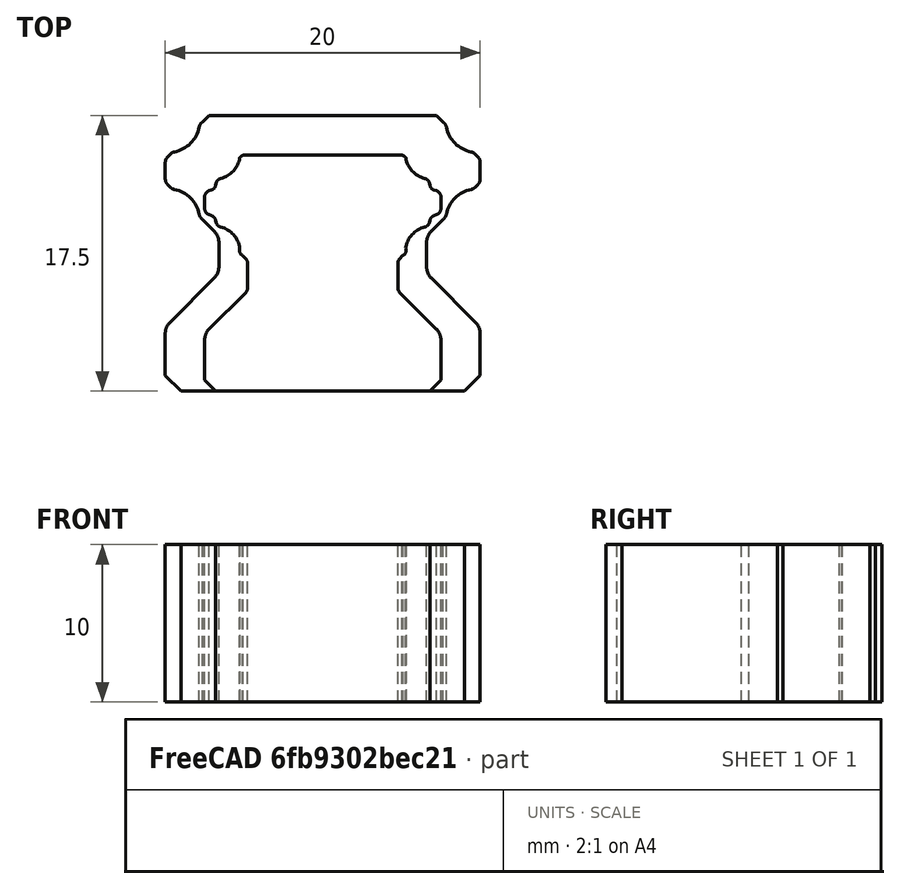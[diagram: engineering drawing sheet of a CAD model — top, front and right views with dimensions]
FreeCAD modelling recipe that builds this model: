
FCSTD DOCUMENT  (FreeCAD 0.20R30923 (Git))
Label: HGxx_temp
License: All rights reserved
LicenseURL: http://en.wikipedia.org/wiki/All_rights_reserved
objects: Sketcher::SketchObject×3, PartDesign::Body×3, App::FeaturePython×2, Part::FeaturePython×2, PartDesign::Pad×2, App::Link×1, Spreadsheet::Sheet×1
note: 13 computed .brp shape members not serialized (recipe doc carries the construction recipe); baked Part::Feature solids carry a one-line shape summary decoded from their .brp

FEATURE [Sketcher::SketchObject] Sketch  label="HGR25R"
  FullyConstrained = false
  TreeRank = 161
  sketch-geometry (46):
    g0: LineSegment StartX=11.2096 StartY=6.56184 StartZ=0 EndX=8.20598 EndY=9.58663 EndZ=0
    g1: LineSegment StartX=-9.97922 StartY=0 StartZ=0 EndX=-11.5 EndY=1.52786 EndZ=0
    g2: LineSegment StartX=-8.20846 StartY=13.8135 StartZ=0 EndX=-8.93873 EndY=14.5438 EndZ=0
    g3: LineSegment StartX=2.10672 StartY=0 StartZ=0 EndX=1.58064 EndY=0.526074 EndZ=0
    g4: LineSegment StartX=-11.2036 StartY=16.7216 StartZ=0 EndX=-11.3536 EndY=16.8716 EndZ=0
    g5: LineSegment StartX=11.3536 StartY=18.9781 StartZ=0 EndX=11.1895 EndY=19.1421 EndZ=0
    g6: LineSegment StartX=9.04575 StartY=21.2544 StartZ=0 EndX=8.30011 EndY=22 EndZ=0
    g7: LineSegment StartX=-9.97922 StartY=0 StartZ=0 EndX=-2.10672 EndY=0 EndZ=0
    g8: LineSegment StartX=2.10672 StartY=0 StartZ=0 EndX=9.97922 EndY=0 EndZ=0
    g9: LineSegment StartX=-1.58064 StartY=0.526074 StartZ=0 EndX=1.58064 EndY=0.526074 EndZ=0
    g10: LineSegment StartX=-8.30011 StartY=22 StartZ=0 EndX=8.30011 EndY=22 EndZ=0
    g11: LineSegment StartX=-2.10672 StartY=0 StartZ=0 EndX=-1.58064 EndY=0.526074 EndZ=0
    g12: LineSegment StartX=11.2036 StartY=16.7216 StartZ=0 EndX=11.3536 EndY=16.8716 EndZ=0
    g13: LineSegment StartX=-11.3536 StartY=18.9781 StartZ=0 EndX=-11.1895 EndY=19.1421 EndZ=0
    g14: LineSegment StartX=-9.04575 StartY=21.2544 StartZ=0 EndX=-8.30011 EndY=22 EndZ=0
    g15: LineSegment StartX=8.20846 StartY=13.8135 StartZ=0 EndX=8.93873 EndY=14.5438 EndZ=0
    g16: LineSegment StartX=9.97922 StartY=0 StartZ=0 EndX=11.5 EndY=1.52786 EndZ=0
    g17: LineSegment StartX=-11.2096 StartY=6.56184 StartZ=0 EndX=-8.20598 EndY=9.58663 EndZ=0
    g18: LineSegment StartX=-11.5 StartY=17.2251 StartZ=0 EndX=-11.5 EndY=18.6245 EndZ=0
    g19: LineSegment StartX=-11.5 StartY=1.52786 StartZ=0 EndX=-11.5 EndY=5.85723 EndZ=0
    g20: LineSegment StartX=-7.91557 StartY=10.2912 StartZ=0 EndX=-7.91557 EndY=13.1064 EndZ=0
    g21: LineSegment StartX=7.91557 StartY=10.2912 StartZ=0 EndX=7.91557 EndY=13.1064 EndZ=0
    g22: LineSegment StartX=11.5 StartY=1.52786 StartZ=0 EndX=11.5 EndY=5.85723 EndZ=0
    g23: LineSegment StartX=11.5 StartY=17.2251 StartZ=0 EndX=11.5 EndY=18.6245 EndZ=0
    g24: ArcOfCircle CenterX=-11.4771 CenterY=14.2438 CenterZ=0 NormalX=0 NormalY=0 NormalZ=1 AngleXU=0 Radius=2.4 StartAngle=0.218097 EndAngle=1.35284
    g25: ArcOfCircle CenterX=-11.4693 CenterY=21.6085 CenterZ=0 NormalX=0 NormalY=0 NormalZ=1 AngleXU=0 Radius=2.4 StartAngle=4.93215 EndAngle=6.08802
    g26: ArcOfCircle CenterX=-11 CenterY=17.2251 CenterZ=0 NormalX=0 NormalY=0 NormalZ=1 AngleXU=0 Radius=0.5 StartAngle=3.14159 EndAngle=3.92699
    g27: ArcOfCircle CenterX=-11 CenterY=18.6245 CenterZ=0 NormalX=0 NormalY=0 NormalZ=1 AngleXU=0 Radius=0.499999 StartAngle=2.3562 EndAngle=3.14159
    g28: ArcOfCircle CenterX=-10.85 CenterY=17.0752 CenterZ=0 NormalX=0 NormalY=0 NormalZ=1 AngleXU=0 Radius=0.5 StartAngle=3.92699 EndAngle=4.49444
    g29: ArcOfCircle CenterX=-10.8494 CenterY=18.7757 CenterZ=0 NormalX=0 NormalY=0 NormalZ=1 AngleXU=0 Radius=0.5 StartAngle=1.76548 EndAngle=2.31906
    g30: ArcOfCircle CenterX=-10.5 CenterY=5.85723 CenterZ=0 NormalX=0 NormalY=0 NormalZ=1 AngleXU=0 Radius=0.999997 StartAngle=2.35971 EndAngle=3.14159
    g31: ArcOfCircle CenterX=-8.91557 CenterY=13.1064 CenterZ=0 NormalX=0 NormalY=0 NormalZ=1 AngleXU=0 Radius=1 StartAngle=0 EndAngle=0.785398
    g32: ArcOfCircle CenterX=-8.91557 CenterY=10.2912 CenterZ=0 NormalX=0 NormalY=0 NormalZ=1 AngleXU=0 Radius=0.999997 StartAngle=5.5013 EndAngle=6.28319
    g33: ArcOfCircle CenterX=-8.67937 CenterY=14.9712 CenterZ=0 NormalX=0 NormalY=0 NormalZ=1 AngleXU=0 Radius=0.5 StartAngle=3.57106 EndAngle=4.16705
    g34: ArcOfCircle CenterX=-8.6749 CenterY=20.9471 CenterZ=0 NormalX=0 NormalY=0 NormalZ=1 AngleXU=0 Radius=0.48161 StartAngle=2.44968 EndAngle=2.72251
    g35: ArcOfCircle CenterX=8.6749 CenterY=20.9471 CenterZ=0 NormalX=0 NormalY=0 NormalZ=1 AngleXU=0 Radius=0.481608 StartAngle=0.419083 EndAngle=0.691918
    g36: ArcOfCircle CenterX=8.67937 CenterY=14.9712 CenterZ=0 NormalX=0 NormalY=0 NormalZ=1 AngleXU=0 Radius=0.5 StartAngle=5.25773 EndAngle=5.85371
    g37: ArcOfCircle CenterX=8.91557 CenterY=10.2912 CenterZ=0 NormalX=0 NormalY=0 NormalZ=1 AngleXU=0 Radius=0.999997 StartAngle=3.14159 EndAngle=3.92348
    g38: ArcOfCircle CenterX=8.91557 CenterY=13.1064 CenterZ=0 NormalX=0 NormalY=0 NormalZ=1 AngleXU=0 Radius=1 StartAngle=2.35619 EndAngle=3.14159
    g39: ArcOfCircle CenterX=10.5 CenterY=5.85723 CenterZ=0 NormalX=0 NormalY=0 NormalZ=1 AngleXU=0 Radius=0.999997 StartAngle=0 EndAngle=0.781885
    g40: ArcOfCircle CenterX=10.8494 CenterY=18.7757 CenterZ=0 NormalX=0 NormalY=0 NormalZ=1 AngleXU=0 Radius=0.5 StartAngle=0.82253 EndAngle=1.37611
    g41: ArcOfCircle CenterX=10.85 CenterY=17.0752 CenterZ=0 NormalX=0 NormalY=0 NormalZ=1 AngleXU=0 Radius=0.5 StartAngle=4.93034 EndAngle=5.49779
    g42: ArcOfCircle CenterX=11 CenterY=17.2251 CenterZ=0 NormalX=0 NormalY=0 NormalZ=1 AngleXU=0 Radius=0.499999 StartAngle=5.49779 EndAngle=6.28319
    g43: ArcOfCircle CenterX=11 CenterY=18.6245 CenterZ=0 NormalX=0 NormalY=0 NormalZ=1 AngleXU=0 Radius=0.5 StartAngle=6.28318 EndAngle=7.06858
    g44: ArcOfCircle CenterX=11.4693 CenterY=21.6085 CenterZ=0 NormalX=0 NormalY=0 NormalZ=1 AngleXU=0 Radius=2.4 StartAngle=3.33676 EndAngle=4.49263
    g45: ArcOfCircle CenterX=11.4771 CenterY=14.2438 CenterZ=0 NormalX=0 NormalY=0 NormalZ=1 AngleXU=0 Radius=2.4 StartAngle=1.78875 EndAngle=2.9235
FEATURE [Sketcher::SketchObject] Sketch001  label="HGR20R"
  FullyConstrained = false
  TreeRank = 159
  sketch-geometry (42):
    g0: LineSegment StartX=-9 StartY=0 StartZ=0 EndX=-10 EndY=1 EndZ=0
    g1: LineSegment StartX=9.70711 StartY=4.36361 StartZ=0 EndX=6.89289 EndY=7.17783 EndZ=0
    g2: LineSegment StartX=-9.69063 StartY=12.9499 StartZ=0 EndX=-9.85355 EndY=13.1128 EndZ=0
    g3: LineSegment StartX=7.63253 StartY=17.0982 StartZ=0 EndX=7.23072 EndY=17.5 EndZ=0
    g4: LineSegment StartX=-6.89289 StartY=10.1522 StartZ=0 EndX=-7.63016 EndY=10.8894 EndZ=0
    g5: LineSegment StartX=9.85355 StartY=14.8772 StartZ=0 EndX=9.6785 EndY=15.0522 EndZ=0
    g6: LineSegment StartX=-9 StartY=0 StartZ=0 EndX=9 EndY=0 EndZ=0
    g7: LineSegment StartX=-7.23072 StartY=17.5 StartZ=0 EndX=7.23072 EndY=17.5 EndZ=0
    g8: LineSegment StartX=-9.85355 StartY=14.8772 StartZ=0 EndX=-9.6785 EndY=15.0522 EndZ=0
    g9: LineSegment StartX=6.89289 StartY=10.1522 StartZ=0 EndX=7.63016 EndY=10.8894 EndZ=0
    g10: LineSegment StartX=9 StartY=0 StartZ=0 EndX=10 EndY=1 EndZ=0
    g11: LineSegment StartX=-9.70711 StartY=4.36361 StartZ=0 EndX=-6.89289 EndY=7.17783 EndZ=0
    g12: LineSegment StartX=9.69063 StartY=12.9499 StartZ=0 EndX=9.85355 EndY=13.1128 EndZ=0
    g13: LineSegment StartX=-7.63253 StartY=17.0982 StartZ=0 EndX=-7.23072 EndY=17.5 EndZ=0
    g14: LineSegment StartX=-10 StartY=1 StartZ=0 EndX=-10 EndY=3.65651 EndZ=0
    g15: LineSegment StartX=-10 StartY=13.4664 StartZ=0 EndX=-10 EndY=14.5236 EndZ=0
    g16: LineSegment StartX=-6.6 StartY=7.88493 StartZ=0 EndX=-6.6 EndY=9.44506 EndZ=0
    g17: LineSegment StartX=6.6 StartY=7.88493 StartZ=0 EndX=6.6 EndY=9.44507 EndZ=0
    g18: LineSegment StartX=10 StartY=1 StartZ=0 EndX=10 EndY=3.65651 EndZ=0
    g19: LineSegment StartX=10 StartY=13.4664 StartZ=0 EndX=10 EndY=14.5236 EndZ=0
    g20: ArcOfCircle CenterX=-9.8106 CenterY=10.8487 CenterZ=0 NormalX=0 NormalY=0 NormalZ=1 AngleXU=0 Radius=2 StartAngle=0.190564 EndAngle=1.38023
    g21: ArcOfCircle CenterX=-9.81014 CenterY=17.1511 CenterZ=0 NormalX=0 NormalY=0 NormalZ=1 AngleXU=0 Radius=2 StartAngle=4.9077 EndAngle=6.08787
    g22: ArcOfCircle CenterX=-9.5 CenterY=13.4664 CenterZ=0 NormalX=0 NormalY=0 NormalZ=1 AngleXU=0 Radius=0.499999 StartAngle=3.14159 EndAngle=3.92699
    g23: ArcOfCircle CenterX=-9.5 CenterY=14.5236 CenterZ=0 NormalX=0 NormalY=0 NormalZ=1 AngleXU=0 Radius=0.499999 StartAngle=2.3562 EndAngle=3.14159
    g24: ArcOfCircle CenterX=-9.33707 CenterY=13.3035 CenterZ=0 NormalX=0 NormalY=0 NormalZ=1 AngleXU=0 Radius=0.499999 StartAngle=3.92699 EndAngle=4.52183
    g25: ArcOfCircle CenterX=-9.32495 CenterY=14.6987 CenterZ=0 NormalX=0 NormalY=0 NormalZ=1 AngleXU=0 Radius=0.500001 StartAngle=1.76611 EndAngle=2.3562
    g26: ArcOfCircle CenterX=-9 CenterY=3.65651 CenterZ=0 NormalX=0 NormalY=0 NormalZ=1 AngleXU=0 Radius=1 StartAngle=2.35619 EndAngle=3.14159
    g27: ArcOfCircle CenterX=-7.6 CenterY=7.88493 CenterZ=0 NormalX=0 NormalY=0 NormalZ=1 AngleXU=0 Radius=1 StartAngle=5.49779 EndAngle=6.28319
    g28: ArcOfCircle CenterX=-7.6 CenterY=9.44506 CenterZ=0 NormalX=0 NormalY=0 NormalZ=1 AngleXU=0 Radius=1 StartAngle=0 EndAngle=0.785399
    g29: ArcOfCircle CenterX=-7.35468 CenterY=16.6825 CenterZ=0 NormalX=0 NormalY=0 NormalZ=1 AngleXU=0 Radius=0.5 StartAngle=2.16 EndAngle=2.97992
    g30: ArcOfCircle CenterX=-7.35293 CenterY=11.3055 CenterZ=0 NormalX=0 NormalY=0 NormalZ=1 AngleXU=0 Radius=0.5 StartAngle=3.29825 EndAngle=4.12467
    g31: ArcOfCircle CenterX=7.35293 CenterY=11.3055 CenterZ=0 NormalX=0 NormalY=0 NormalZ=1 AngleXU=0 Radius=0.5 StartAngle=5.30011 EndAngle=6.12653
    g32: ArcOfCircle CenterX=7.35468 CenterY=16.6825 CenterZ=0 NormalX=0 NormalY=0 NormalZ=1 AngleXU=0 Radius=0.500001 StartAngle=0.161676 EndAngle=0.981596
    g33: ArcOfCircle CenterX=7.6 CenterY=7.88493 CenterZ=0 NormalX=0 NormalY=0 NormalZ=1 AngleXU=0 Radius=1 StartAngle=3.14159 EndAngle=3.92699
    g34: ArcOfCircle CenterX=7.6 CenterY=9.44507 CenterZ=0 NormalX=0 NormalY=0 NormalZ=1 AngleXU=0 Radius=1 StartAngle=2.35619 EndAngle=3.14159
    g35: ArcOfCircle CenterX=9 CenterY=3.65651 CenterZ=0 NormalX=0 NormalY=0 NormalZ=1 AngleXU=0 Radius=1 StartAngle=0 EndAngle=0.785398
    g36: ArcOfCircle CenterX=9.32495 CenterY=14.6987 CenterZ=0 NormalX=0 NormalY=0 NormalZ=1 AngleXU=0 Radius=0.499999 StartAngle=0.785397 EndAngle=1.37548
    g37: ArcOfCircle CenterX=9.33707 CenterY=13.3035 CenterZ=0 NormalX=0 NormalY=0 NormalZ=1 AngleXU=0 Radius=0.5 StartAngle=4.90295 EndAngle=5.49779
    g38: ArcOfCircle CenterX=9.5 CenterY=13.4664 CenterZ=0 NormalX=0 NormalY=0 NormalZ=1 AngleXU=0 Radius=0.499999 StartAngle=5.49779 EndAngle=6.28319
    g39: ArcOfCircle CenterX=9.5 CenterY=14.5236 CenterZ=0 NormalX=0 NormalY=0 NormalZ=1 AngleXU=0 Radius=0.499999 StartAngle=0 EndAngle=0.785397
    g40: ArcOfCircle CenterX=9.81014 CenterY=17.1511 CenterZ=0 NormalX=0 NormalY=0 NormalZ=1 AngleXU=0 Radius=2 StartAngle=3.33691 EndAngle=4.51707
    g41: ArcOfCircle CenterX=9.8106 CenterY=10.8487 CenterZ=0 NormalX=0 NormalY=0 NormalZ=1 AngleXU=0 Radius=2 StartAngle=1.76136 EndAngle=2.95103
  constraints (50):
    c: Coincident(g7,g13)
    c: Coincident(g13,g29)
    c: Coincident(g21,g29)
    c: Coincident(g21,g25)
    c: Coincident(g8,g25)
    c: Coincident(g8,g23)
    c: Coincident(g15,g23)
    c: Coincident(g15,g22)
    c: Coincident(g2,g22)
    c: Coincident(g2,g24)
    c: Coincident(g20,g24)
    c: Coincident(g20,g30)
    c: Coincident(g4,g30)
    c: Coincident(g4,g28)
    c: Coincident(g16,g28)
    c: Coincident(g16,g27)
    c: Coincident(g11,g27)
    c: Coincident(g11,g26)
    c: Coincident(g14,g26)
    c: Coincident(g0,g14)
    c: Coincident(g0,g6)
    c: Coincident(g6,g10)
    c: Coincident(g10,g18)
    c: Coincident(g18,g35)
    c: Coincident(g1,g35)
    c: Coincident(g1,g33)
    c: Coincident(g17,g33)
    c: Coincident(g17,g34)
    c: Coincident(g9,g34)
    c: Coincident(g9,g31)
    c: Coincident(g31,g41)
    c: Coincident(g37,g41)
    c: Coincident(g12,g37)
    c: Coincident(g12,g38)
    c: Coincident(g19,g38)
    c: Coincident(g19,g39)
    c: Coincident(g5,g39)
    c: Coincident(g5,g36)
    c: Coincident(g36,g40)
    c: Coincident(g32,g40)
    c: Coincident(g3,g32)
    c: Coincident(g3,g7)
    c: Horizontal(g7)
    c: Vertical(g19)
    c: Vertical(g18)
    c: Horizontal(g6)
    c: Vertical(g16)
    c: Vertical(g17)
    c: Vertical(g14)
    c: Vertical(g15)
FEATURE [Sketcher::SketchObject] Sketch002  label="HGR15R"
  FullyConstrained = false
  TreeRank = 158
  sketch-geometry (50):
    g0: LineSegment StartX=6.80531 StartY=13.0612 StartZ=0 EndX=6.77501 EndY=13.2021 EndZ=0
    g1: LineSegment StartX=-6.77426 StartY=10.7128 StartZ=0 EndX=-6.80624 EndY=10.8541 EndZ=0
    g2: LineSegment StartX=-6.8 StartY=0 StartZ=0 EndX=-7.5 EndY=0.7 EndZ=0
    g3: LineSegment StartX=7.20711 StartY=3.95047 StartZ=0 EndX=4.88716 EndY=6.27042 EndZ=0
    g4: LineSegment StartX=-4.88716 StartY=8.39816 StartZ=0 EndX=-5.08159 EndY=8.59259 EndZ=0
    g5: LineSegment StartX=5.08606 StartY=14.9629 StartZ=0 EndX=5.04899 EndY=15 EndZ=0
    g6: LineSegment StartX=-7.06065 StartY=11.1421 StartZ=0 EndX=-7.23572 EndY=11.2052 EndZ=0
    g7: LineSegment StartX=7.21871 StartY=12.7195 StartZ=0 EndX=7.07767 EndY=12.7633 EndZ=0
    g8: LineSegment StartX=-6.8 StartY=0 StartZ=0 EndX=6.8 EndY=0 EndZ=0
    g9: LineSegment StartX=-5.04899 StartY=15 StartZ=0 EndX=5.04899 EndY=15 EndZ=0
    g10: LineSegment StartX=-7.21871 StartY=12.7195 StartZ=0 EndX=-7.07767 EndY=12.7633 EndZ=0
    g11: LineSegment StartX=7.06065 StartY=11.1421 StartZ=0 EndX=7.23572 EndY=11.2052 EndZ=0
    g12: LineSegment StartX=6.8 StartY=0 StartZ=0 EndX=7.5 EndY=0.7 EndZ=0
    g13: LineSegment StartX=-7.20711 StartY=3.95047 StartZ=0 EndX=-4.88716 EndY=6.27042 EndZ=0
    g14: LineSegment StartX=4.88716 StartY=8.39816 StartZ=0 EndX=5.08159 EndY=8.59259 EndZ=0
    g15: LineSegment StartX=-5.08606 StartY=14.9629 StartZ=0 EndX=-5.04899 EndY=15 EndZ=0
    g16: LineSegment StartX=6.77426 StartY=10.7128 StartZ=0 EndX=6.80623 EndY=10.8541 EndZ=0
    g17: LineSegment StartX=-6.80531 StartY=13.0612 StartZ=0 EndX=-6.77501 EndY=13.2021 EndZ=0
    g18: LineSegment StartX=-7.5 StartY=0.7 StartZ=0 EndX=-7.5 EndY=3.24336 EndZ=0
    g19: LineSegment StartX=-7.5 StartY=11.5815 StartZ=0 EndX=-7.5 EndY=12.3375 EndZ=0
    g20: LineSegment StartX=-4.77 StartY=6.55326 StartZ=0 EndX=-4.77 EndY=8.11532 EndZ=0
    g21: LineSegment StartX=4.77 StartY=6.55326 StartZ=0 EndX=4.77 EndY=8.11532 EndZ=0
    g22: LineSegment StartX=7.5 StartY=0.7 StartZ=0 EndX=7.5 EndY=3.24336 EndZ=0
    g23: LineSegment StartX=7.5 StartY=11.5815 StartZ=0 EndX=7.5 EndY=12.3375 EndZ=0
    g24: ArcOfCircle CenterX=-7.19637 CenterY=10.7658 CenterZ=0 NormalX=0 NormalY=0 NormalZ=1 AngleXU=0 Radius=0.4 StartAngle=0.222511 EndAngle=1.22461
    g25: ArcOfCircle CenterX=-7.19637 CenterY=13.1453 CenterZ=0 NormalX=0 NormalY=0 NormalZ=1 AngleXU=0 Radius=0.399999 StartAngle=5.01369 EndAngle=6.07137
    g26: ArcOfCircle CenterX=-7.1 CenterY=11.5815 CenterZ=0 NormalX=0 NormalY=0 NormalZ=1 AngleXU=0 Radius=0.4 StartAngle=3.14159 EndAngle=4.3662
    g27: ArcOfCircle CenterX=-7.1 CenterY=12.3375 CenterZ=0 NormalX=0 NormalY=0 NormalZ=1 AngleXU=0 Radius=0.399999 StartAngle=1.8721 EndAngle=3.14159
    g28: ArcOfCircle CenterX=-6.85624 CenterY=8.85756 CenterZ=0 NormalX=0 NormalY=0 NormalZ=1 AngleXU=0 Radius=1.6 StartAngle=0.134276 EndAngle=1.33249
    g29: ArcOfCircle CenterX=-6.85623 CenterY=15.0614 CenterZ=0 NormalX=0 NormalY=0 NormalZ=1 AngleXU=0 Radius=1.6 StartAngle=4.95078 EndAngle=6.13385
    g30: ArcOfCircle CenterX=-6.5 CenterY=3.24336 CenterZ=0 NormalX=0 NormalY=0 NormalZ=1 AngleXU=0 Radius=1 StartAngle=2.35619 EndAngle=3.14159
    g31: ArcOfCircle CenterX=-6.38412 CenterY=10.801 CenterZ=0 NormalX=0 NormalY=0 NormalZ=1 AngleXU=0 Radius=0.4 StartAngle=3.3641 EndAngle=4.47408
    g32: ArcOfCircle CenterX=-6.38395 CenterY=13.118 CenterZ=0 NormalX=0 NormalY=0 NormalZ=1 AngleXU=0 Radius=0.4 StartAngle=1.80919 EndAngle=2.92978
    g33: ArcOfCircle CenterX=-5.17 CenterY=6.55326 CenterZ=0 NormalX=0 NormalY=0 NormalZ=1 AngleXU=0 Radius=0.4 StartAngle=5.49779 EndAngle=6.28319
    g34: ArcOfCircle CenterX=-5.17 CenterY=8.11532 CenterZ=0 NormalX=0 NormalY=0 NormalZ=1 AngleXU=0 Radius=0.4 StartAngle=0 EndAngle=0.785398
    g35: ArcOfCircle CenterX=-4.95206 CenterY=14.586 CenterZ=0 NormalX=0 NormalY=0 NormalZ=1 AngleXU=0 Radius=0.4 StartAngle=1.91239 EndAngle=2.50636
    g36: ArcOfCircle CenterX=-4.89142 CenterY=8.9445 CenterZ=0 NormalX=0 NormalY=0 NormalZ=1 AngleXU=0 Radius=0.4 StartAngle=2.81782 EndAngle=4.21695
    g37: ArcOfCircle CenterX=4.89142 CenterY=8.9445 CenterZ=0 NormalX=0 NormalY=0 NormalZ=1 AngleXU=0 Radius=0.4 StartAngle=5.20783 EndAngle=6.60695
    g38: ArcOfCircle CenterX=4.95206 CenterY=14.586 CenterZ=0 NormalX=0 NormalY=0 NormalZ=1 AngleXU=0 Radius=0.4 StartAngle=0.635234 EndAngle=1.2292
    g39: ArcOfCircle CenterX=5.17 CenterY=6.55326 CenterZ=0 NormalX=0 NormalY=0 NormalZ=1 AngleXU=0 Radius=0.4 StartAngle=3.14159 EndAngle=3.92699
    g40: ArcOfCircle CenterX=5.17 CenterY=8.11532 CenterZ=0 NormalX=0 NormalY=0 NormalZ=1 AngleXU=0 Radius=0.4 StartAngle=2.3562 EndAngle=3.14159
    g41: ArcOfCircle CenterX=6.38395 CenterY=13.118 CenterZ=0 NormalX=0 NormalY=0 NormalZ=1 AngleXU=0 Radius=0.399999 StartAngle=0.211816 EndAngle=1.33241
    g42: ArcOfCircle CenterX=6.38412 CenterY=10.801 CenterZ=0 NormalX=0 NormalY=0 NormalZ=1 AngleXU=0 Radius=0.4 StartAngle=4.9507 EndAngle=6.06068
    g43: ArcOfCircle CenterX=6.5 CenterY=3.24336 CenterZ=0 NormalX=0 NormalY=0 NormalZ=1 AngleXU=0 Radius=1 StartAngle=0 EndAngle=0.785398
    g44: ArcOfCircle CenterX=6.85623 CenterY=15.0614 CenterZ=0 NormalX=0 NormalY=0 NormalZ=1 AngleXU=0 Radius=1.6 StartAngle=3.29093 EndAngle=4.474
    g45: ArcOfCircle CenterX=6.85624 CenterY=8.85756 CenterZ=0 NormalX=0 NormalY=0 NormalZ=1 AngleXU=0 Radius=1.6 StartAngle=1.8091 EndAngle=3.00732
    g46: ArcOfCircle CenterX=7.1 CenterY=11.5815 CenterZ=0 NormalX=0 NormalY=0 NormalZ=1 AngleXU=0 Radius=0.4 StartAngle=5.05857 EndAngle=6.28319
    g47: ArcOfCircle CenterX=7.1 CenterY=12.3375 CenterZ=0 NormalX=0 NormalY=0 NormalZ=1 AngleXU=0 Radius=0.4 StartAngle=1.15308e-06 EndAngle=1.2695
    g48: ArcOfCircle CenterX=7.19637 CenterY=10.7658 CenterZ=0 NormalX=0 NormalY=0 NormalZ=1 AngleXU=0 Radius=0.4 StartAngle=1.91698 EndAngle=2.91908
    g49: ArcOfCircle CenterX=7.19637 CenterY=13.1453 CenterZ=0 NormalX=0 NormalY=0 NormalZ=1 AngleXU=0 Radius=0.4 StartAngle=3.35341 EndAngle=4.41109
  constraints (50):
    c: Coincident(g9,g15)
    c: Coincident(g15,g35)
    c: Coincident(g29,g35)
    c: Coincident(g29,g32)
    c: Coincident(g17,g32)
    c: Coincident(g17,g25)
    c: Coincident(g10,g25)
    c: Coincident(g10,g27)
    c: Coincident(g19,g27)
    c: Coincident(g19,g26)
    c: Coincident(g6,g26)
    c: Coincident(g6,g24)
    c: Coincident(g1,g24)
    c: Coincident(g1,g31)
    c: Coincident(g28,g31)
    c: Coincident(g28,g36)
    c: Coincident(g4,g36)
    c: Coincident(g4,g34)
    c: Coincident(g20,g34)
    c: Coincident(g20,g33)
    c: Coincident(g13,g33)
    c: Coincident(g13,g30)
    c: Coincident(g18,g30)
    c: Coincident(g2,g18)
    c: Coincident(g2,g8)
    c: Coincident(g8,g12)
    c: Coincident(g12,g22)
    c: Coincident(g22,g43)
    c: Coincident(g3,g43)
    c: Coincident(g3,g39)
    c: Coincident(g21,g39)
    c: Coincident(g21,g40)
    c: Coincident(g14,g40)
    c: Coincident(g14,g37)
    c: Coincident(g37,g45)
    c: Coincident(g42,g45)
    c: Coincident(g16,g42)
    c: Coincident(g16,g48)
    c: Coincident(g11,g48)
    c: Coincident(g11,g46)
    c: Coincident(g23,g46)
    c: Coincident(g23,g47)
    c: Coincident(g7,g47)
    c: Coincident(g7,g49)
    c: Coincident(g0,g49)
    c: Coincident(g0,g41)
    c: Coincident(g41,g44)
    c: Coincident(g38,g44)
    c: Coincident(g5,g38)
    c: Coincident(g5,g9)
FEATURE [App::FeaturePython] Constraints  # WARN: FeaturePython — macro-defined, semantics opaque (R4)
  TreeRank = 163
  _LinkVersion = 1
  _Version = 1
FEATURE [App::FeaturePython] Elements  # WARN: FeaturePython — macro-defined, semantics opaque (R4)
  TreeRank = 164
  _LinkVersion = 1
FEATURE [App::Link] Link  label="Link(HGR15)"
  AutoLinkLabel = false
  AutoPlacement = true
  LinkTransform = true
  LinkedObject = -> Body001
  SyncGroupVisibility = false
  TreeRank = 166
  _LinkVersion = 1
  expr: LinkedObject = Spreadsheet.HGRresult
FEATURE [Part::FeaturePython] Parts  # WARN: FeaturePython — macro-defined, semantics opaque (R4)
  Group = -> [Link]
  GroupMode = 0
  TreeRank = 165
  _LinkVersion = 1
FEATURE [Part::FeaturePython] Assembly  # WARN: FeaturePython — macro-defined, semantics opaque (R4)
  AutoRelax = true
  BuildShape = 0
  Configuration = 1
  Freeze = false
  Group = -> [Constraints,Elements,Parts]
  TreeRank = 162
  Verbose = false
  _LinkVersion = 1
  _SolverType = 1
  _Version = 1
  expr: Configuration.Enum = Spreadsheet.cells[<<A3:|>>]
FEATURE [PartDesign::Body] Body003  label="HGR25"
  AutoGroupSolids = false
  ExportMode = 0
  Group = -> [Sketch]
  Origin = -> Origin003
  TreeRank = 196
  _ExportChildren = -> [Sketch]
  _GroupVersion = 1
FEATURE [PartDesign::Pad] Pad002
  AddSubType = 0
  AlongSketchNormal = false
  CheckUpToFaceLimits = true
  ClaimChildren = false
  Direction = (0,0,1)
  Fit = 0
  FitJoin = 0
  InnerFit = 0
  InnerFitJoin = 0
  InnerTaperAngle = 0
  InnerTaperAngleRev = 0
  Length = 10
  Length2 = 100
  Linearize = true
  NewSolid = false
  Profile = -> Sketch002
  Suppress = false
  TreeRank = 199
  Type = 0
  _ProfileBasedVersion = 1
FEATURE [PartDesign::Body] Body001  label="HGR15"
  AutoGroupSolids = false
  ExportMode = 0
  Group = -> [Sketch002,Pad002]
  Origin = -> Origin001
  Tip = -> Pad002
  TreeRank = 176
  _ExportChildren = -> [Pad002]
  _GroupVersion = 1
FEATURE [PartDesign::Pad] Pad003
  AddSubType = 0
  AlongSketchNormal = false
  CheckUpToFaceLimits = true
  ClaimChildren = false
  Direction = (0,0,1)
  Fit = 0
  FitJoin = 0
  InnerFit = 0
  InnerFitJoin = 0
  InnerTaperAngle = 0
  InnerTaperAngleRev = 0
  Length = 10
  Length2 = 100
  Linearize = true
  NewSolid = false
  Profile = -> Sketch001
  Suppress = false
  TreeRank = 200
  Type = 0
  _ProfileBasedVersion = 1
FEATURE [PartDesign::Body] Body002  label="HGR20"
  AutoGroupSolids = false
  ExportMode = 0
  Group = -> [Sketch001,Pad003]
  Origin = -> Origin002
  Tip = -> Pad003
  TreeRank = 186
  _ExportChildren = -> [Pad003]
  _GroupVersion = 1
FEATURE [Spreadsheet::Sheet] Spreadsheet
  PythonMode = false
  ShowCells = 0
  TreeRank = 201
  cells = A2==dbind(Assembly.Configuration.All); B2(HGRnumber)==.B4; A3=HGR15; B3=1; A4=HGR20; B4=2; A5=HGR25; B5=3; A8(HGR_str)==.HGRnumber == 1 ? <<HGR15>> : (.HGRnumber == 2 ? <<HGR20>> : <<HGR25>>); A9(HGRresult)==<<Body00%s (%s)>> % tuple(.HGRnumber, HGR_str)
  expr: cells.Bind.B2.ZZ2 = tuple(.cells, <<B>> + str(hiddenref(Assembly.Configuration) + 3), <<ZZ>> + str(hiddenref(Assembly.Configuration) + 3))
